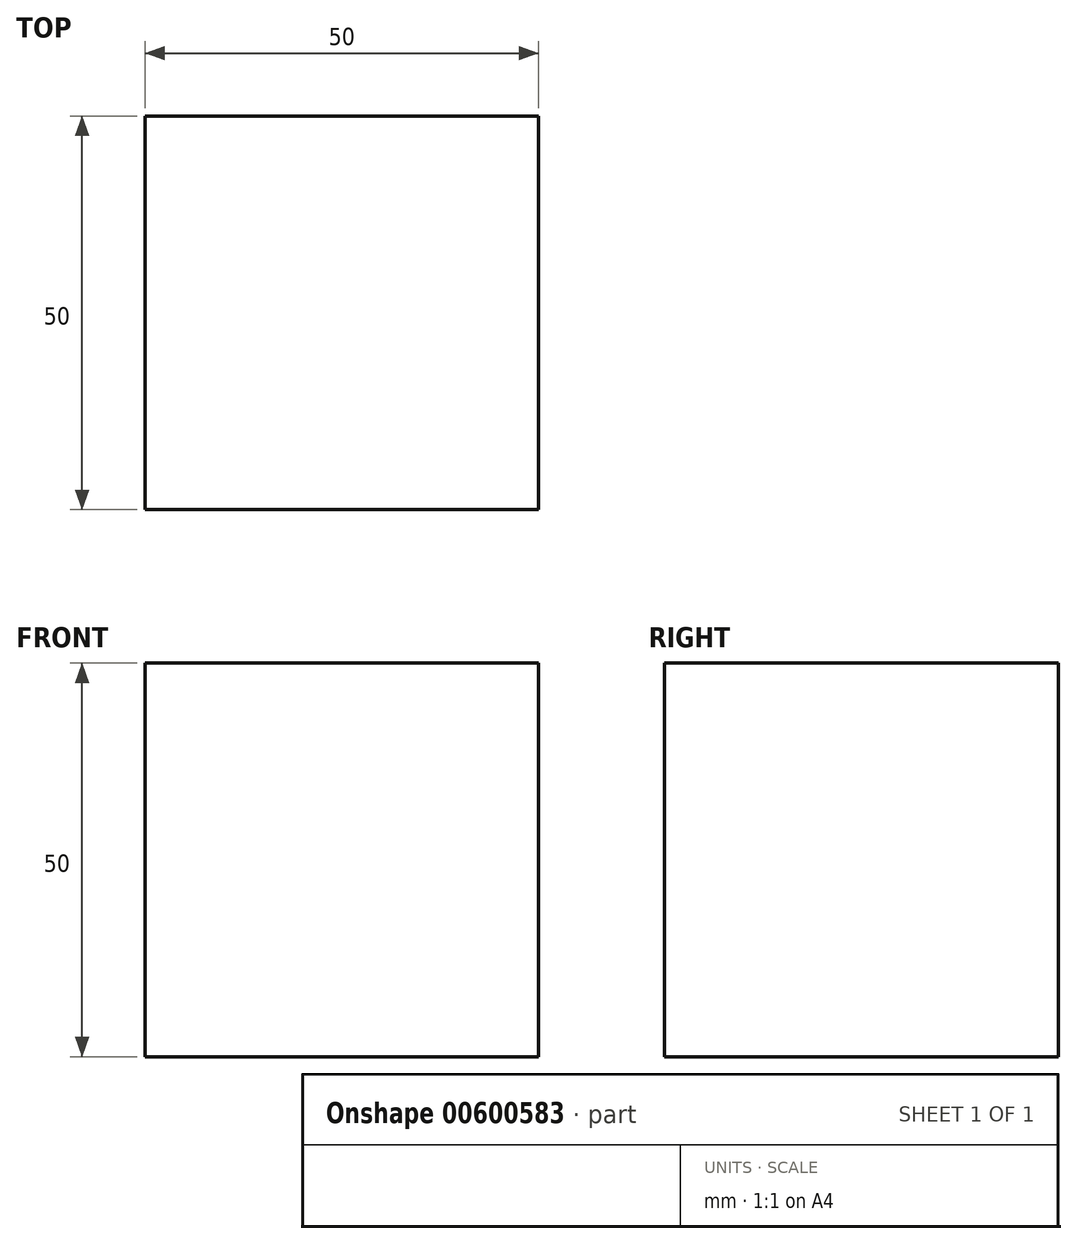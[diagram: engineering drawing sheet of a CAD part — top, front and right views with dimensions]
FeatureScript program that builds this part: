
annotation { "Feature Type Name" : "Feature", "Feature Type Description" : "" }
export const myFeature = defineFeature(function(context is Context, id is Id, definition is map)
    precondition{}
    {
        {
            var Q0;
            Q0=qCreatedBy(makeId("Top.planeOp"),FACE);
            var sketch = newSketch(context, id + "F0", { "sketchPlane" : qUnion([Q0])});
            skLineSegment(sketch, "E0.bottom", {"start": v(25, -25) * mm, "end": v(-25, -25) * mm});
            skLineSegment(sketch, "E0.top", {"start": v(25, 25) * mm, "end": v(-25, 25) * mm});
            skLineSegment(sketch, "E0.left", {"start": v(25, -25) * mm, "end": v(25, 25) * mm});
            skLineSegment(sketch, "E0.right", {"start": v(-25, -25) * mm, "end": v(-25, 25) * mm});
            skPoint(sketch, "E0.middle", {"position": v(0, 0) * mm});
            skSolve(sketch);
        }
        {
            var Q0;
            Q0 = qSketchRegion(id + "F0", true);
            extrude(context, id + "F1", {"entities" : qUnion([Q0]), "endBound" : BoundingType.SYMMETRIC, "depth" : 50 * mm, "offsetDistance" : 25 * mm});
        }
    });
